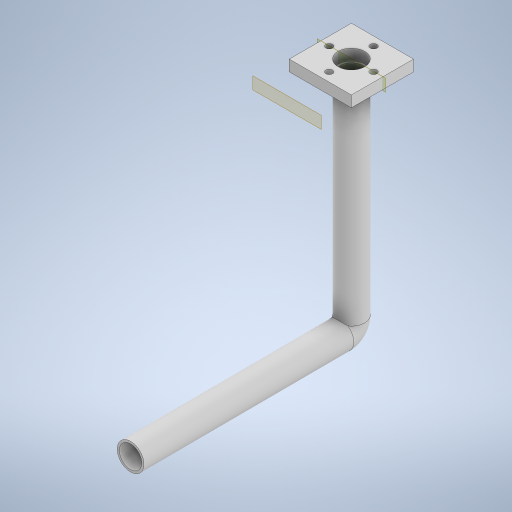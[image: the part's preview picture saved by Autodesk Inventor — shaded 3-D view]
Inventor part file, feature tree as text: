
AUTODESK INVENTOR PART (.ipt)
format: ipt  version: 2023 (Build 270158000, 158)  size: 311,296 bytes
history: native  units: mm
features: sketch x6, extrude x2, plane x2, sweep x1, chamfer x1
ambient origin geometry x8: Origin, YZ Plane, XZ Plane, XY Plane, X Axis, Y Axis, Z Axis, Center Point
bodies: Solid1 (feature_tree)
feature tree (12):
  extrude  "Extrusion1"  Depth=28.0mm
  extrude  "Extrusion2"  Depth=14.0mm
  plane  "Work Plane1"
  sketch  "Sketch3"  dims[d4=5.0mm d5=0.0mm d6=12.0mm]
  sketch  "3D Sketch1"
  sketch  "3D Sketch2"
  sweep  "Sweep1"
  chamfer  "Chamfer1"  Distance=10.0mm
  plane  "Work Plane2"
  sketch  "Sketch1"  dims[d0=28.0mm d1=28.0mm]
  sketch  "Sketch2"  dims[d2=14.0mm d3=14.0mm]
  sketch  "Sketch4"  dims[d7=3.0mm d8=10.0mm d9=40.0mm d11=360.0deg d13=5.0mm d14=0.0mm d15=-14.0mm d16=100.0mm d17=100.0mm d18=5.0mm d19=10.0mm d20=0.0mm d21=0.0mm d22=12.0mm d23=1.0mm d24=2.0mm d25=45.0deg d44=15.0mm d29=0.0mm d30=0.0mm d31=0.0mm d32=0.0mm]
